# Revit family: Sensor-Lutron-Radio_Powr_Savr_Ceiling_Occupancy_and_Vacancy
name_source: partatom
category: Lighting Devices
revit_build: Autodesk Revit 2017 (Build: 20160720_1515(x64)
units: mm (PartAtom-declared; Revit-internal decimal feet)

## family parameters
Cut with Voids When Loaded = No
Host = Face
Maintain Annotation Orientation = No
OmniClass Number = 23.85.80.11.27
OmniClass Title = Lighting Controls
Part Type = Normal
Room Calculation Point = No
Round Connector Dimension = Use Diameter
Shared = No

## types (2) — shared parameters
Assembly Code = D5030800
Ceiling Opening Diameter = 0' - 3"
Ceiling Opening Radius = 0' - 1 1/2"
Current = 14 mA
Default Elevation = 0' - 0"
Description = Wireless Ceiling Mount Sensor
Field of View = 360.00°
Frequency = 434 MHz
Instruction Sheet Link = http://www.lutron.com
Light Level = 1 fc
Manufacturer = Lutron Electronics Co., Inc
Manufacturer Fax Number = 610-282-1243
Maximum Ceiling Height = 12' - 0"
Maximum Coverage = 676.00 SF
Maximum Operating Temperature = 104 °F
Maximum Room Coverage (L x W) = 12ft x 12ft
Minimum Ceiling Height = 8' - 0"
Minimum Clearance = 4' - 0"
Minimum Coverage = 324.00 SF
Minimum Operating Temperature = 32 °F
Minimum Room Coverage (L x W) = 8ft x 8ft
Mounting Diameter = 0' - 2 27/32"
Mounting Radius = 0' - 1 7/16"
Overall Depth = 0' - 3 9/16"
Overall Width = 0' - 1 1/8"
Performance URL = http://www.lutron.com
Product Documentation Link = http://www.lutron.com
Product Name = Wireless Ceiling Mount Sensor
Product Page URL = http://www.lutron.com
Radius of Coverage at Floor = 13' - 0"
Sensor Body Height = 0' - 0 1/2"
Sensor Cover Offset = 0' - 0 7/8"
Sensor Diameter = 0' - 1 1/2"
Sensor Material = Plastic - Lutron - White
Sensor Radius = 0' - 0 3/4"
Series = Radio Powr Savr
URL = http://www.lutron.com
Version = 2017 - v1.0b
Video Link = https://www.youtube.com
Voltage = 3 V
Warranty URL = http://www.lutron.com
zero-valued in all types: Cost

## per-type parameters (varying)
| type | Label | Occupancy Sensor | Vacancy Sensor |
| LRF2-VCR2B-P-WH | VS | No | Yes |
| LRF2-OCR2B-P-WH | OS | Yes | No |

note: column(s) folded — value = type name in every type: Model

## geometry (parser evidence)
native form markers: Blend x8, Sweep x9
no freeform markers — native parametric forms only
